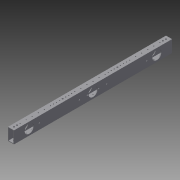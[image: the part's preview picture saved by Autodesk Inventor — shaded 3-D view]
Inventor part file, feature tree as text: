
AUTODESK INVENTOR PART (.ipt)
format: ipt  version: 2015 SP1 (Build 190203100, 203)  size: 308,224 bytes
history: native  units: in
note: dims shown in document units (in); Inventor stores cm internally (conversion verified against a paired STEP export)
features: sketch x8, projected_geometry x7, hole x5, extrude x3, pattern_linear x1
ambient origin geometry x8: Origin, YZ Plane, XZ Plane, XY Plane, X Axis, Y Axis, Z Axis, Center Point
bodies: Solid1 (feature_tree)
feature tree (24):
  extrude  "Extrusion1"  Depth=2.0in
  hole  "Hole1"  [1 undecoded]
  pattern_linear  "Rectangular Pattern1"  Count1=26 Spacing1=1.0in
  hole  "Hole2"  [1 undecoded]
  hole  "Hole3"  [1 undecoded]
  hole  "Hole4"  [1 undecoded]
  extrude  "Extrusion2"  Depth=1.0in
  hole  "Hole5"  [1 undecoded]
  extrude  "Extrusion4"  Depth=2.0in
  sketch  "Sketch1"  dims[d0=1.0in d1=2.0in]
  sketch  "Sketch2"  dims[d2=1.8in d3=0.8in]
  projected_geometry  "Projected Loop1"
  sketch  "Sketch3"  dims[d4=0.1in]
  projected_geometry  "Projected Loop2"
  sketch  "Sketch4"  dims[d5=0.1in]
  projected_geometry  "Projected Loop3"
  sketch  "Sketch5"  dims[d6=26.0in d7=0.0in]
  projected_geometry  "Projected Loop4"
  sketch  "Sketch6"  dims[d8=0.5in]
  projected_geometry  "Projected Loop5"
  sketch  "Sketch7"  dims[d9=0.5in]
  projected_geometry  "Projected Loop6"
  sketch  "Sketch9"  dims[d10=0.1562in d11=0.75in d12=0.375in d13=0.25in d14=0.5635in d15=1.0in d16=0.8108in d17=10.2362in d19=1.0in d20=2.5in d21=1.0in d22=2.5in d23=1.0in d24=1.0in d25=13.0in d26=1.5in d27=0.75in d28=0.375in d29=0.25in d30=0.5635in d31=1.0in d32=0.8108in d33=2.25in d34=2.25in d35=1.0in d36=1.0in d37=1.0in d38=1.0in d39=0.9375in d40=0.9375in d41=0.19in d42=0.75in d43=0.375in d44=0.25in d45=0.5635in d46=1.0in d47=0.8108in d48=1.0in d49=1.0in d50=4.1562in d51=4.1562in d52=0.19in d53=0.75in d54=0.375in d55=0.25in d56=0.5635in d57=1.0in d58=0.8108in d59=0.25in d60=0.25in d61=1.0in d62=0.5in d63=0.25in d64=1.0in d65=0.5in d66=0.25in d67=2.0in d68=0.0in d69=7.0in d70=8.0in d71=9.0in d72=10.0in d73=0.5in d74=0.5in d75=0.5in d76=0.5in d77=0.5in d78=0.5in d79=0.5in d80=0.5in d81=7.0in d82=8.0in d83=9.0in d84=10.0in d85=0.1562in d86=0.75in d87=0.375in d88=0.25in d89=0.5635in d90=1.0in d91=0.8108in d98=0.25in d99=0.25in d100=2.0in d101=0.0in]
  projected_geometry  "Projected Loop8"
note: 5 required parameter values undecoded (feature->parameter linkage not recoverable at this tier; creation-order binding heuristic only, values carry confidence <= 0.55)
